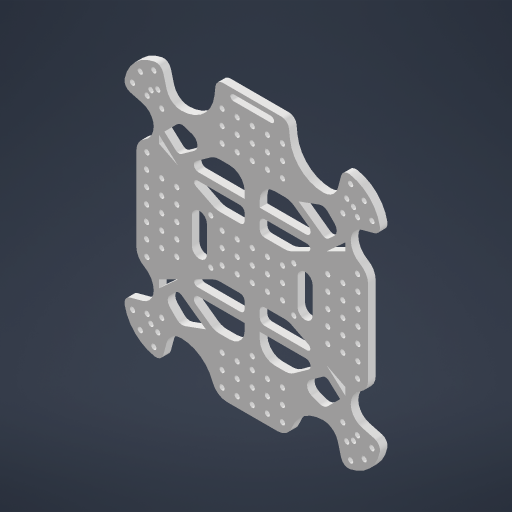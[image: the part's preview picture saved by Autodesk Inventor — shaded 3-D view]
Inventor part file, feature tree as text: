
AUTODESK INVENTOR PART (.ipt)
format: ipt  version: 2023 (Build 270158000, 158)  size: 978,432 bytes
history: native  units: mm
features: fillet x10, other x9, extrude x7, sketch x5, reference x4
ambient origin geometry x8: Origin, YZ Plane, XZ Plane, XY Plane, X Axis, Y Axis, Z Axis, Center Point
bodies: Solid1 (feature_tree)
feature tree (35):
  other  "Base Sketch With Dimensions"
  extrude  "Extrusion1"  TaperAngle=30.0deg  [1 undecoded]
  fillet  "Fillet1"  [1 undecoded]
  sketch  "Sketch3"  dims[d0=3.5mm d1=30.0deg d2=30.0deg]
  extrude  "Side Extensions"  TaperAngle=30.0deg  [1 undecoded]
  extrude  "Bottom Holes"  TaperAngle=30.0deg  [1 undecoded]
  fillet  "Fillet2"  Radius=45.0mm
  extrude  "ESC holders"  Depth=25.0mm
  extrude  "Hole Countersinks"  TaperAngle=135.0deg  [1 undecoded]
  extrude  "Skeleton"  TaperAngle=135.0deg  [1 undecoded]
  fillet  "Fillet3"  Radius=20.0mm
  fillet  "Fillet4"  Radius=120.0mm
  fillet  "Fillet5"  Radius=120.0mm
  fillet  "Fillet6"  Radius=25.0mm
  fillet  "Fillet8"  Radius=5.0mm
  fillet  "Fillet9"  Radius=5.0mm
  fillet  "Fillet10"  Radius=10.0mm
  fillet  "Fillet11"  Radius=10.0mm
  extrude  "Extrusion9"  Depth=10.0mm
  reference  "Reference1"
  reference  "Reference2"
  reference  "Reference3"
  reference  "Reference4"
  sketch  "Sketch4"  dims[d3=20.0mm d5=30.0deg d6=30.0deg]
  other  "Skeleton Sketch"
  sketch  "Sketch6"  dims[d9=30.0deg d10=30.0deg d13=30.0deg d14=30.0deg d16=45.0mm]
  sketch  "Sketch7"  dims[d17=140.0mm d18=25.0mm]
  sketch  "Sketch8"  dims[d19=70.0mm d23=135.0deg d25=135.0deg d29=20.0mm d30=120.0mm d32=120.0mm d40=25.0mm d41=5.0mm d44=5.0mm d45=0.0mm d46=10.0mm d80=50.0mm d82=10.0mm d83=30.0mm d85=10.0mm d88=50.0mm d90=10.0mm d91=30.0mm d93=10.0mm d97=5.0mm d98=50.0mm d102=10.0mm d103=0.0mm d104=17.5mm d105=0.0mm d106=70.0mm d107=10.0mm d108=50.0mm d109=30.0mm d134=3.5mm d135=0.5mm d136=0.5mm d137=30.0mm d138=30.0mm d139=25.0mm d140=0.0mm d151=6.5mm d152=50.0mm d154=10.0mm d155=30.0mm d157=10.0mm d160=30.0mm d162=10.0mm d163=50.0mm d165=10.0mm d168=50.0mm d170=10.0mm d171=30.0mm d173=10.0mm d176=30.0mm d178=10.0mm d179=50.0mm d181=10.0mm d184=50.0mm d186=10.0mm d187=30.0mm d189=10.0mm d192=2.0mm d193=0.0mm d204=5.0mm d205=5.0mm d206=5.0mm d207=5.0mm d208=2.0mm d209=0.0mm d210=5.0mm d211=5.0mm d212=5.0mm d213=2.0mm d214=10.0mm d216=5.0mm d217=5.0mm d218=5.0mm d220=5.0mm d221=10.0mm d222=15.0mm d223=5.0mm d225=5.0mm d227=10.0mm d228=3.0mm d229=50.0mm d230=30.0mm d232=10.0mm d233=50.0mm d235=10.0mm d238=3.5mm d239=100.0mm d240=5.0mm d241=5.0mm d242=5.0mm d243=3.0mm d244=4.0mm d246=25.0mm d247=10.0mm d248=5.0mm d249=15.0mm d250=15.0mm d252=3.5mm d253=27.5mm d254=27.5mm d255=85.0mm d256=10.0mm d257=0.0mm d258=140.0mm d259=0.0mm d260=0.0mm d261=0.0mm]
  parser-record x1  (decoder bookkeeping rows leaked as tree rows — omitted from the tree; the rows remain in map.json)
  other  "total.iam"
  other  "_arm:3"
  other  "body holder:1"
  other  "_arm:4"
  other  "_arm:2"
  other  "_arm:1"
note: 6 required parameter values undecoded (feature->parameter linkage not recoverable at this tier; creation-order binding heuristic only, values carry confidence <= 0.55)
note: 1 file-system path scrubbed to <path> (originals preserved in map.json)
